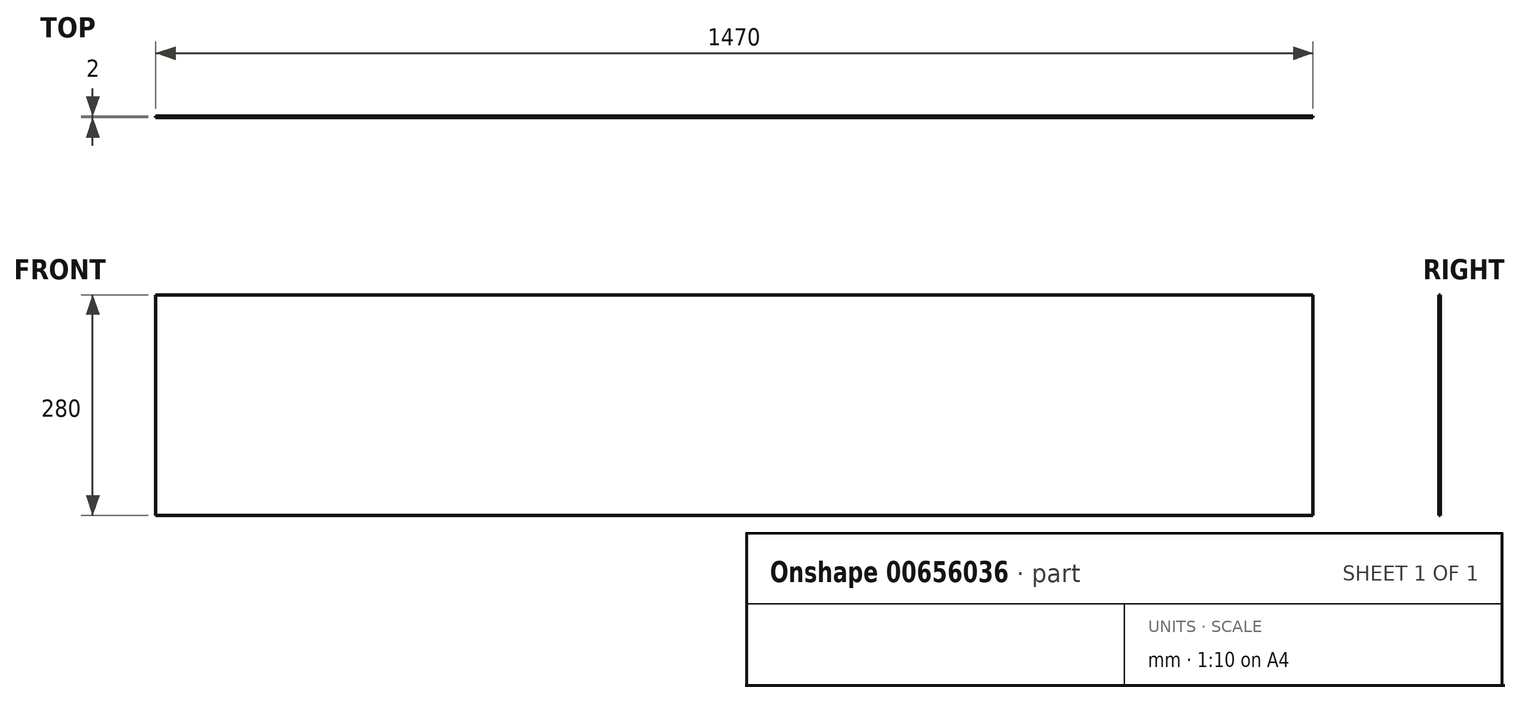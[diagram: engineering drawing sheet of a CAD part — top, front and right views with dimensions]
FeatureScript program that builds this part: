
annotation { "Feature Type Name" : "Feature", "Feature Type Description" : "" }
export const myFeature = defineFeature(function(context is Context, id is Id, definition is map)
    precondition{}
    {
        {
            var Q0;
            Q0=qCreatedBy(makeId("Front.planeOp"),FACE);
            var sketch = newSketch(context, id + "F0", { "sketchPlane" : qUnion([Q0])});
            skLineSegment(sketch, "E0.bottom", {"start": v(735, -140) * mm, "end": v(-735, -140) * mm});
            skLineSegment(sketch, "E0.top", {"start": v(735, 140) * mm, "end": v(-735, 140) * mm});
            skLineSegment(sketch, "E0.left", {"start": v(735, -140) * mm, "end": v(735, 140) * mm});
            skLineSegment(sketch, "E0.right", {"start": v(-735, -140) * mm, "end": v(-735, 140) * mm});
            skPoint(sketch, "E0.middle", {"position": v(0, 0) * mm});
            skSolve(sketch);
        }
        {
            var Q0;
            Q0=makeQuery(id+"F0.imprint","IMPRINT",FACE,{"disambiguationData":[TD([[makeQuery(id+"F0.imprint","IMPRINT",EDGE,{"derivedFrom":sQuery(id+"F0.wireOp",EDGE,"E0.bottom")}),-1.0]])]});
            extrude(context, id + "F1", {"entities" : qUnion([Q0]), "depth" : 2 * mm, "offsetDistance" : 25.4 * mm});
        }
    });
